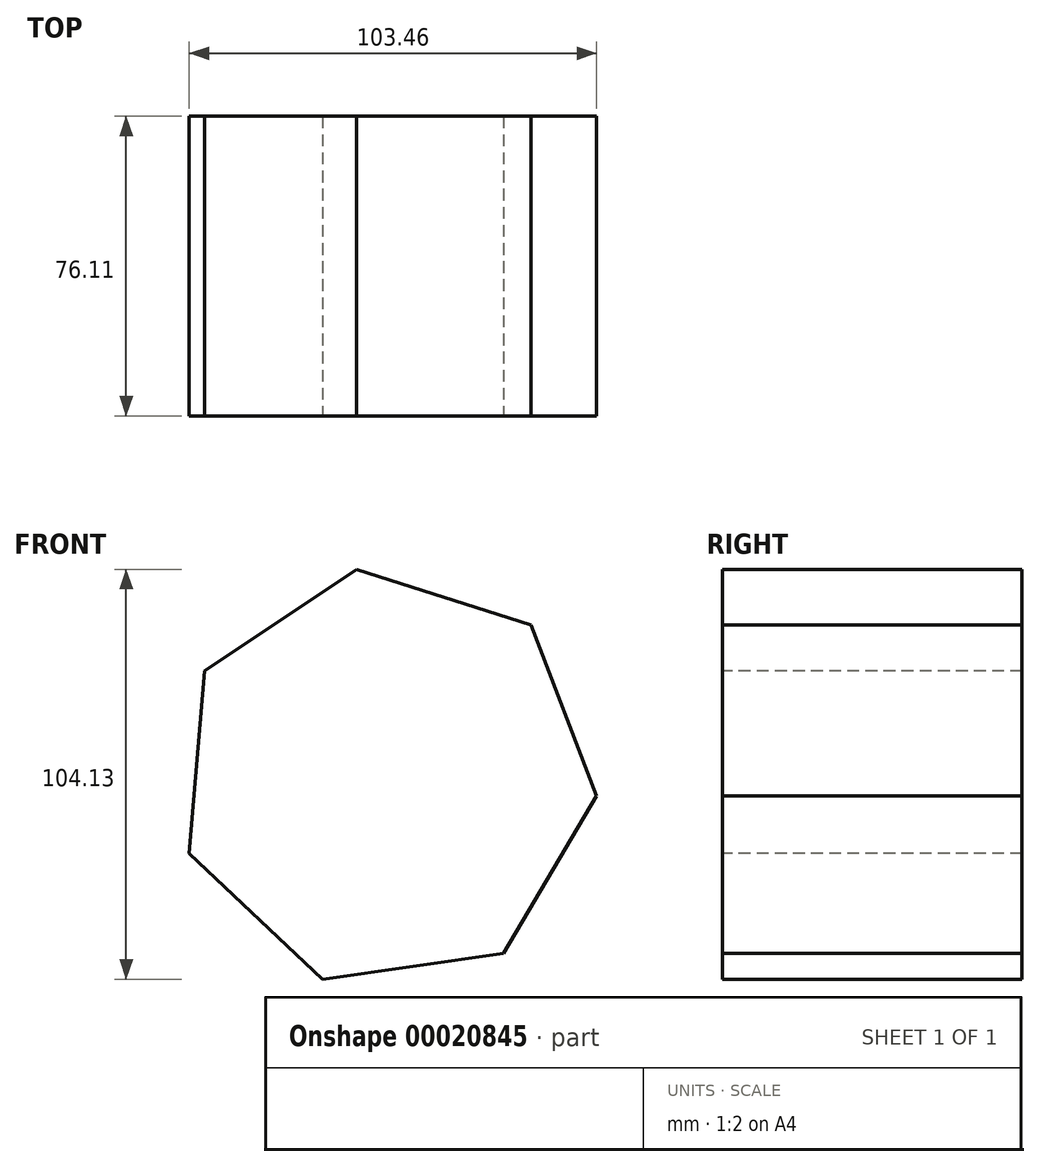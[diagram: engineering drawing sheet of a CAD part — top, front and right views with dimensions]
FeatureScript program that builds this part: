
annotation { "Feature Type Name" : "Feature", "Feature Type Description" : "" }
export const myFeature = defineFeature(function(context is Context, id is Id, definition is map)
    precondition{}
    {
        {
            var Q0;
            Q0=qCreatedBy(makeId("Front.planeOp"),FACE);
            var sketch = newSketch(context, id + "F0", { "sketchPlane" : qUnion([Q0])});
            skLineSegment(sketch, "E0.bottom", {"start": v(-10, 24.84) * mm, "end": v(11.79, 24.84) * mm});
            skLineSegment(sketch, "E0.top", {"start": v(-10, -20.3) * mm, "end": v(11.79, -20.3) * mm});
            skLineSegment(sketch, "E0.left", {"start": v(-10, 24.84) * mm, "end": v(-10, -20.3) * mm});
            skLineSegment(sketch, "E0.right", {"start": v(11.79, 24.84) * mm, "end": v(11.79, -20.3) * mm});
            skCircle(sketch, "E1.cCircle", {"center": v(-16.79, 15.38) * mm, "radius": 48.28 * mm, "construction": true});
            skLineSegment(sketch, "E1.0", {"start": v(13.02, -29.16) * mm, "end": v(-33.02, -35.7) * mm});
            skLineSegment(sketch, "E1.1", {"start": v(-33.02, -35.7) * mm, "end": v(-66.84, -3.77) * mm});
            skLineSegment(sketch, "E1.2", {"start": v(-66.84, -3.77) * mm, "end": v(-62.97, 42.57) * mm});
            skLineSegment(sketch, "E1.3", {"start": v(-62.97, 42.57) * mm, "end": v(-24.32, 68.44) * mm});
            skLineSegment(sketch, "E1.4", {"start": v(-24.32, 68.44) * mm, "end": v(20, 54.35) * mm});
            skLineSegment(sketch, "E1.5", {"start": v(20, 54.35) * mm, "end": v(36.62, 10.92) * mm});
            skLineSegment(sketch, "E1.6", {"start": v(36.62, 10.92) * mm, "end": v(13.02, -29.16) * mm});
            skPoint(sketch, "E1.0.midPoint", {"position": v(-10, -32.42) * mm});
            skSolve(sketch);
        }
        {
            var Q0;
            Q0 = qSketchRegion(id + "F0", true);
            var Q1;
            Q1=makeQuery(id+"F0.imprint","IMPRINT",FACE,{"disambiguationData":[TD([[makeQuery(id+"F0.imprint","IMPRINT",EDGE,{"derivedFrom":sQuery(id+"F0.wireOp",EDGE,"E0.bottom")}),-1.0]])]});
            extrude(context, id + "F1", {"entities" : qUnion([Q0, Q1]), "oppositeDirection" : true, "depth" : 76.1 * mm});
        }
        {
            var Q0;
            Q0=makeQuery(id+"F1.opExtrude","CAP_FACE",FACE,{"disambiguationData":[OSD([sQuery(id+"F0.wireOp",EDGE,"E1.0"),sQuery(id+"F0.wireOp",EDGE,"E1.1"),sQuery(id+"F0.wireOp",EDGE,"E1.2"),sQuery(id+"F0.wireOp",EDGE,"E1.3"),sQuery(id+"F0.wireOp",EDGE,"E1.4"),sQuery(id+"F0.wireOp",EDGE,"E1.5"),sQuery(id+"F0.wireOp",EDGE,"E1.6")])],"isStart":true});
            var sketch = newSketch(context, id + "F2", { "sketchPlane" : qUnion([Q0])});
            skCircle(sketch, "E2", {"center": v(0, 0) * mm, "radius": 18.22 * mm});
            skSolve(sketch);
        }
        {
            var Q0;
            Q0 = qSketchRegion(id + "F2", true);
            extrude(context, id + "F3", {"entities" : qUnion([Q0]), "operationType" : NewBodyOperationType.ADD, "oppositeDirection" : true, "depth" : 47.67 * mm});
        }
    });
